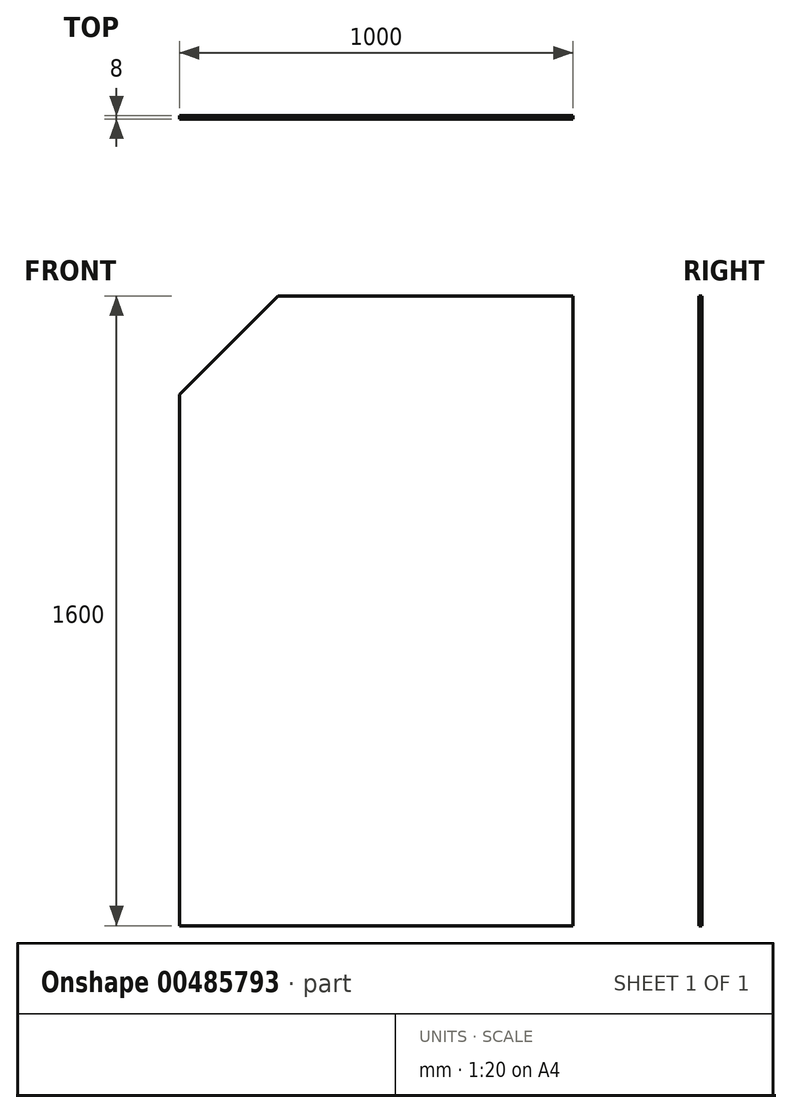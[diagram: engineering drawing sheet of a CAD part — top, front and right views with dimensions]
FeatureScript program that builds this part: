
annotation { "Feature Type Name" : "Feature", "Feature Type Description" : "" }
export const myFeature = defineFeature(function(context is Context, id is Id, definition is map)
    precondition{}
    {
        {
            var Q0;
            Q0=qCreatedBy(makeId("Front.planeOp"),FACE);
            var sketch = newSketch(context, id + "F0", { "sketchPlane" : qUnion([Q0])});
            skLineSegment(sketch, "E0.bottom", {"start": v(500, 800) * mm, "end": v(-500, 800) * mm});
            skLineSegment(sketch, "E0.top", {"start": v(500, -800) * mm, "end": v(-500, -800) * mm});
            skLineSegment(sketch, "E0.left", {"start": v(500, 800) * mm, "end": v(500, -800) * mm});
            skLineSegment(sketch, "E0.right", {"start": v(-500, 800) * mm, "end": v(-500, -800) * mm});
            skPoint(sketch, "E0.middle", {"position": v(0, 0) * mm});
            skLineSegment(sketch, "E1", {"start": v(500, 800) * mm, "end": v(-250, 800) * mm});
            skLineSegment(sketch, "E2", {"start": v(-250, 800) * mm, "end": v(-500, 550) * mm});
            skSolve(sketch);
        }
        {
            var Q0;
            {var subQ1=sQuery(id+"F0.wireOp",EDGE,"E0.top");Q0=makeQuery(id+"F0.imprint","IMPRINT",FACE,{"disambiguationData":[TD([[makeQuery(id+"F0.imprint","IMPRINT",EDGE,{"derivedFrom":subQ1}),-1.0]])]});}
            extrude(context, id + "F1", {"entities" : qUnion([Q0]), "depth" : 8 * mm});
        }
    });
